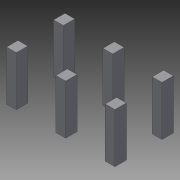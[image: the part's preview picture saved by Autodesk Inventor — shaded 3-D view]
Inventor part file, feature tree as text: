
AUTODESK INVENTOR PART (.ipt)
format: ipt  version: 2015 (Build 190159000, 159)  size: 114,688 bytes
history: native  units: mm
features: other x1, extrude x1, sketch x1
ambient origin geometry x8: Origin, YZ Plane, XZ Plane, XY Plane, X Axis, Y Axis, Z Axis, Center Point
bodies: Body1 (feature_tree)
feature tree (3):
  other  "ソリッド1"
  extrude  "押し出し1"  Depth=0.98mm
  sketch  "スケッチ1"
